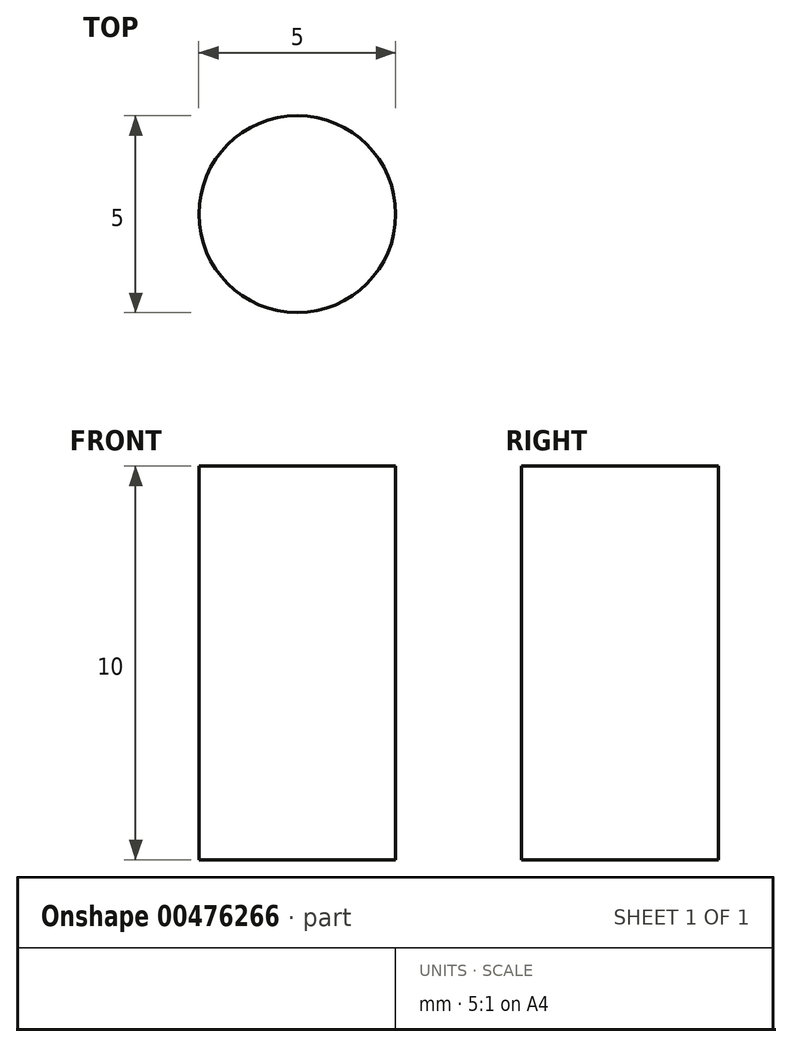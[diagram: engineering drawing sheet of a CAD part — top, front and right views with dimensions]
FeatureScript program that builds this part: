
annotation { "Feature Type Name" : "Feature", "Feature Type Description" : "" }
export const myFeature = defineFeature(function(context is Context, id is Id, definition is map)
    precondition{}
    {
        {
            var Q0;
            Q0=qCreatedBy(makeId("Top.planeOp"),FACE);
            var sketch = newSketch(context, id + "F0", { "sketchPlane" : qUnion([Q0])});
            skCircle(sketch, "E0", {"center": v(-45.29, 42.52) * mm, "radius": 2.5 * mm});
            skSolve(sketch);
        }
        {
            var Q0;
            Q0=makeQuery(id+"F0.imprint","IMPRINT",FACE,{"disambiguationData":[TD([[makeQuery(id+"F0.imprint","IMPRINT",EDGE,{"derivedFrom":sQuery(id+"F0.wireOp",EDGE,"E0")}),1.0]])]});
            extrude(context, id + "F1", {"entities" : qUnion([Q0]), "depth" : 10 * mm, "offsetDistance" : 25 * mm});
        }
    });
